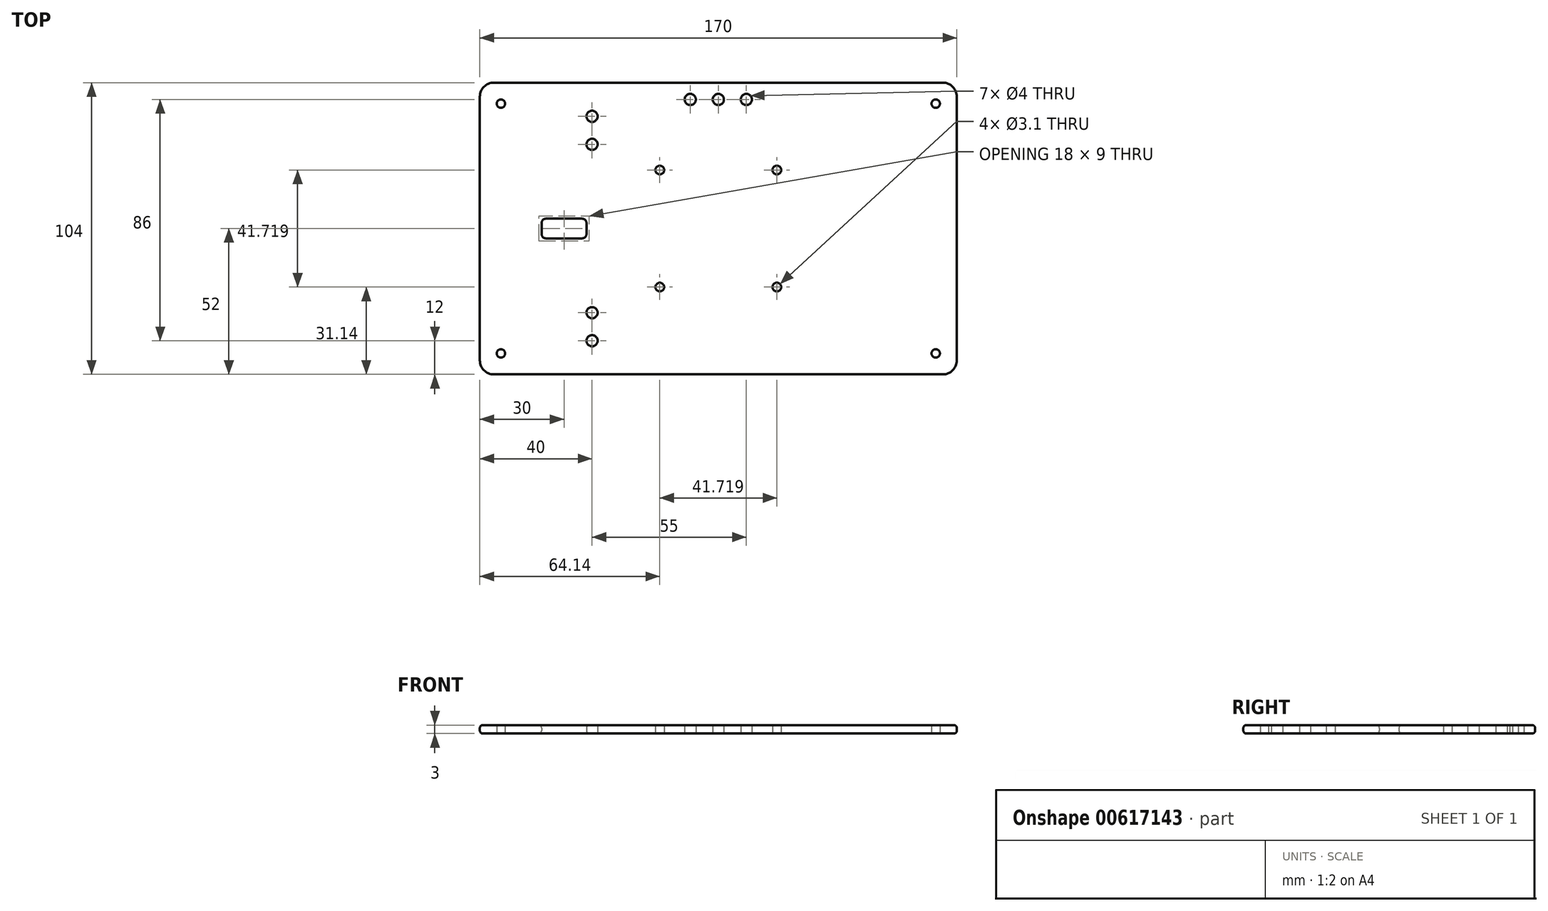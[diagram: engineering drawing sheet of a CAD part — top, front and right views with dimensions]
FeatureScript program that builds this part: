
annotation { "Feature Type Name" : "Feature", "Feature Type Description" : "" }
export const myFeature = defineFeature(function(context is Context, id is Id, definition is map)
    precondition{}
    {
        {
            var Q0;
            Q0=qCreatedBy(makeId("Top.planeOp"),FACE);
            var sketch = newSketch(context, id + "F0", { "sketchPlane" : qUnion([Q0])});
            skCircle(sketch, "E0", {"center": v(-77.5, 44.5) * mm, "radius": 1.5 * mm});
            skCircle(sketch, "E1.MirrorC", {"center": v(77.5, 44.5) * mm, "radius": 1.5 * mm});
            skCircle(sketch, "E2.MirrorC", {"center": v(-77.5, -44.5) * mm, "radius": 1.5 * mm});
            skCircle(sketch, "E3.MirrorC", {"center": v(77.5, -44.5) * mm, "radius": 1.5 * mm});
            skLineSegment(sketch, "E4.bottom", {"start": v(-85, 52) * mm, "end": v(85, 52) * mm});
            skLineSegment(sketch, "E4.top", {"start": v(-85, -52) * mm, "end": v(85, -52) * mm});
            skLineSegment(sketch, "E4.left", {"start": v(-85, 52) * mm, "end": v(-85, -52) * mm});
            skLineSegment(sketch, "E4.right", {"start": v(85, 52) * mm, "end": v(85, -52) * mm});
            skCircle(sketch, "E5", {"center": v(0, 0) * mm, "radius": 29.5 * mm, "construction": true});
            skCircle(sketch, "E6", {"center": v(-20.86, 20.86) * mm, "radius": 1.55 * mm});
            skCircle(sketch, "E7.1.0", {"center": v(-20.86, -20.86) * mm, "radius": 1.55 * mm});
            skCircle(sketch, "E7.2.0", {"center": v(20.86, -20.86) * mm, "radius": 1.55 * mm});
            skCircle(sketch, "E7.3.0", {"center": v(20.86, 20.86) * mm, "radius": 1.55 * mm});
            skCircle(sketch, "E8", {"center": v(0, 0) * mm, "radius": 37.5 * mm, "construction": true});
            skLineSegment(sketch, "E9.bottom", {"start": v(-63, -3.5) * mm, "end": v(-47, -3.5) * mm});
            skLineSegment(sketch, "E9.top", {"start": v(-63, 3.5) * mm, "end": v(-47, 3.5) * mm});
            skLineSegment(sketch, "E9.left", {"start": v(-63, -3.5) * mm, "end": v(-63, 3.5) * mm});
            skLineSegment(sketch, "E9.right", {"start": v(-47, -3.5) * mm, "end": v(-47, 3.5) * mm});
            skPoint(sketch, "E9.middle", {"position": v(-55, 0) * mm});
            skCircle(sketch, "E10", {"center": v(-45, 40) * mm, "radius": 2 * mm});
            skCircle(sketch, "E11", {"center": v(-45, 30) * mm, "radius": 2 * mm});
            skCircle(sketch, "E12.MirrorC", {"center": v(-45, -30) * mm, "radius": 2 * mm});
            skCircle(sketch, "E13.MirrorC", {"center": v(-45, -40) * mm, "radius": 2 * mm});
            skCircle(sketch, "E14", {"center": v(10, 46) * mm, "radius": 2 * mm});
            skCircle(sketch, "E15.MirrorC", {"center": v(-10, 46) * mm, "radius": 2 * mm});
            skCircle(sketch, "E16", {"center": v(0, 46) * mm, "radius": 2 * mm});
            skSolve(sketch);
        }
        {
            var Q0;
            Q0=makeQuery(id+"F0.imprint","IMPRINT",FACE,{"disambiguationData":[TD([[makeQuery(id+"F0.imprint","IMPRINT",EDGE,{"derivedFrom":sQuery(id+"F0.wireOp",EDGE,"E0")}),-1.0]])]});
            extrude(context, id + "F1", {"entities" : qUnion([Q0]), "depth" : 3 * mm});
        }
        {
            var Q0;
            Q0=makeQuery(id+"F1.opExtrude","SWEPT_EDGE",EDGE,{"disambiguationData":[OSD([sQuery(id+"F0.wireOp",EDGE,"E4.top"),sQuery(id+"F0.wireOp",EDGE,"E4.left")])]});
            var Q1;
            Q1=makeQuery(id+"F1.opExtrude","SWEPT_EDGE",EDGE,{"disambiguationData":[OSD([sQuery(id+"F0.wireOp",EDGE,"E4.bottom"),sQuery(id+"F0.wireOp",EDGE,"E4.left")])]});
            var Q2;
            Q2=makeQuery(id+"F1.opExtrude","SWEPT_EDGE",EDGE,{"disambiguationData":[OSD([sQuery(id+"F0.wireOp",EDGE,"E4.bottom"),sQuery(id+"F0.wireOp",EDGE,"E4.right")])]});
            var Q3;
            Q3=makeQuery(id+"F1.opExtrude","SWEPT_EDGE",EDGE,{"disambiguationData":[OSD([sQuery(id+"F0.wireOp",EDGE,"E4.top"),sQuery(id+"F0.wireOp",EDGE,"E4.right")])]});
            fillet(context, id + "F2", {"entities" : qUnion([Q0, Q1, Q2, Q3]), "radius" : 5 * mm, "tangentPropagation" : true, "allowEdgeOverflow" : false});
        }
        {
            var Q0;
            Q0=makeQuery(id+"F1.opExtrude","SWEPT_EDGE",EDGE,{"disambiguationData":[OSD([sQuery(id+"F0.wireOp",EDGE,"E9.top"),sQuery(id+"F0.wireOp",EDGE,"E9.right")])]});
            var Q1;
            Q1=makeQuery(id+"F1.opExtrude","SWEPT_EDGE",EDGE,{"disambiguationData":[OSD([sQuery(id+"F0.wireOp",EDGE,"E9.bottom"),sQuery(id+"F0.wireOp",EDGE,"E9.right")])]});
            var Q2;
            Q2=makeQuery(id+"F1.opExtrude","SWEPT_EDGE",EDGE,{"disambiguationData":[OSD([sQuery(id+"F0.wireOp",EDGE,"E9.bottom"),sQuery(id+"F0.wireOp",EDGE,"E9.left")])]});
            var Q3;
            Q3=makeQuery(id+"F1.opExtrude","SWEPT_EDGE",EDGE,{"disambiguationData":[OSD([sQuery(id+"F0.wireOp",EDGE,"E9.top"),sQuery(id+"F0.wireOp",EDGE,"E9.left")])]});
            fillet(context, id + "F3", {"entities" : qUnion([Q0, Q1, Q2, Q3]), "radius" : 1.5 * mm, "tangentPropagation" : true, "allowEdgeOverflow" : false});
        }
        {
            var Q0;
            Q0=makeQuery(id+"F1.opExtrude","CAP_EDGE",EDGE,{"disambiguationData":[OSD([sQuery(id+"F0.wireOp",EDGE,"E4.bottom")])],"isStart":false});
            var Q1;
            Q1=makeQuery(id+"F1.opExtrude","CAP_EDGE",EDGE,{"disambiguationData":[OSD([sQuery(id+"F0.wireOp",EDGE,"E4.bottom")])],"isStart":true});
            var Q2;
            Q2=makeQuery(id+"F1.opExtrude","CAP_EDGE",EDGE,{"disambiguationData":[OSD([sQuery(id+"F0.wireOp",EDGE,"E9.bottom")])],"isStart":false});
            var Q3;
            Q3=makeQuery(id+"F1.opExtrude","CAP_EDGE",EDGE,{"disambiguationData":[OSD([sQuery(id+"F0.wireOp",EDGE,"E9.top")])],"isStart":true});
            fillet(context, id + "F4", {"entities" : qUnion([Q0, Q1, Q2, Q3]), "radius" : 1 * mm, "tangentPropagation" : true, "allowEdgeOverflow" : false});
        }
    });
